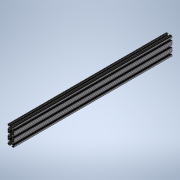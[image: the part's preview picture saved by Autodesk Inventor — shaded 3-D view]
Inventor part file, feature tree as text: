
AUTODESK INVENTOR PART (.ipt)
format: ipt  version: 2020 (Build 240168000, 168)  size: 363,008 bytes
history: native  units: in
note: dims shown in document units (in); Inventor stores cm internally (conversion verified against a paired STEP export)
features: extrude x1, sketch x1
ambient origin geometry x8: Origin, YZ Plane, XZ Plane, XY Plane, X Axis, Y Axis, Z Axis, Center Point
bodies: Solid1 (feature_tree)
feature tree (2):
  extrude  "Extrusion1"  [1 undecoded]
  sketch  "Sketch1"  dims[d0=26.0in d1=0.0in]
note: 1 required parameter value undecoded (feature->parameter linkage not recoverable at this tier; creation-order binding heuristic only, values carry confidence <= 0.55)
